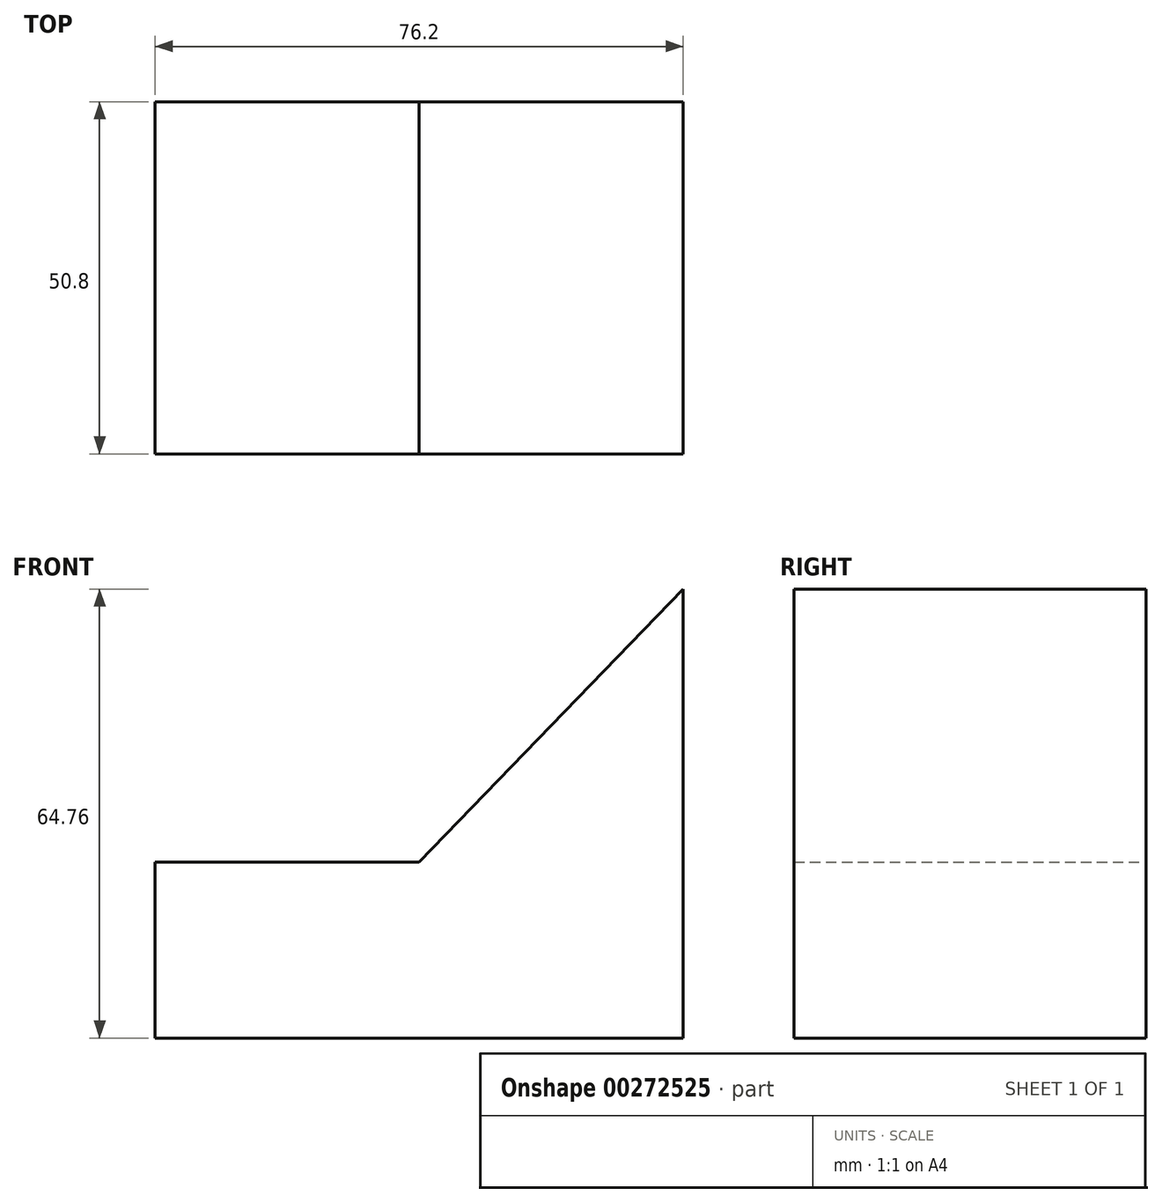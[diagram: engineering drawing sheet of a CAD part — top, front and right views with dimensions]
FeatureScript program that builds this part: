
annotation { "Feature Type Name" : "Feature", "Feature Type Description" : "" }
export const myFeature = defineFeature(function(context is Context, id is Id, definition is map)
    precondition{}
    {
        {
            var Q0;
            Q0=qCreatedBy(makeId("Front.planeOp"),FACE);
            var sketch = newSketch(context, id + "F0", { "sketchPlane" : qUnion([Q0])});
            skLineSegment(sketch, "E0.bottom", {"start": v(0, 0) * mm, "end": v(-76.2, 0) * mm});
            skLineSegment(sketch, "E0.left", {"start": v(0, 0) * mm, "end": v(0, 25.4) * mm});
            skLineSegment(sketch, "E0.right", {"start": v(-76.2, 0) * mm, "end": v(-76.2, 25.4) * mm});
            skLineSegment(sketch, "E1", {"start": v(-76.2, 25.4) * mm, "end": v(-38.1, 25.4) * mm});
            skLineSegment(sketch, "E2", {"start": v(-38.1, 25.4) * mm, "end": v(-11.6, 52.78) * mm});
            skLineSegment(sketch, "E3", {"start": v(-11.6, 52.78) * mm, "end": v(0, 64.76) * mm});
            skLineSegment(sketch, "E4", {"start": v(0, 64.76) * mm, "end": v(0, 25.4) * mm});
            skSolve(sketch);
        }
        {
            var Q0;
            Q0 = qSketchRegion(id + "F0", true);
            extrude(context, id + "F1", {"entities" : qUnion([Q0]), "depth" : 50.8 * mm});
        }
    });
